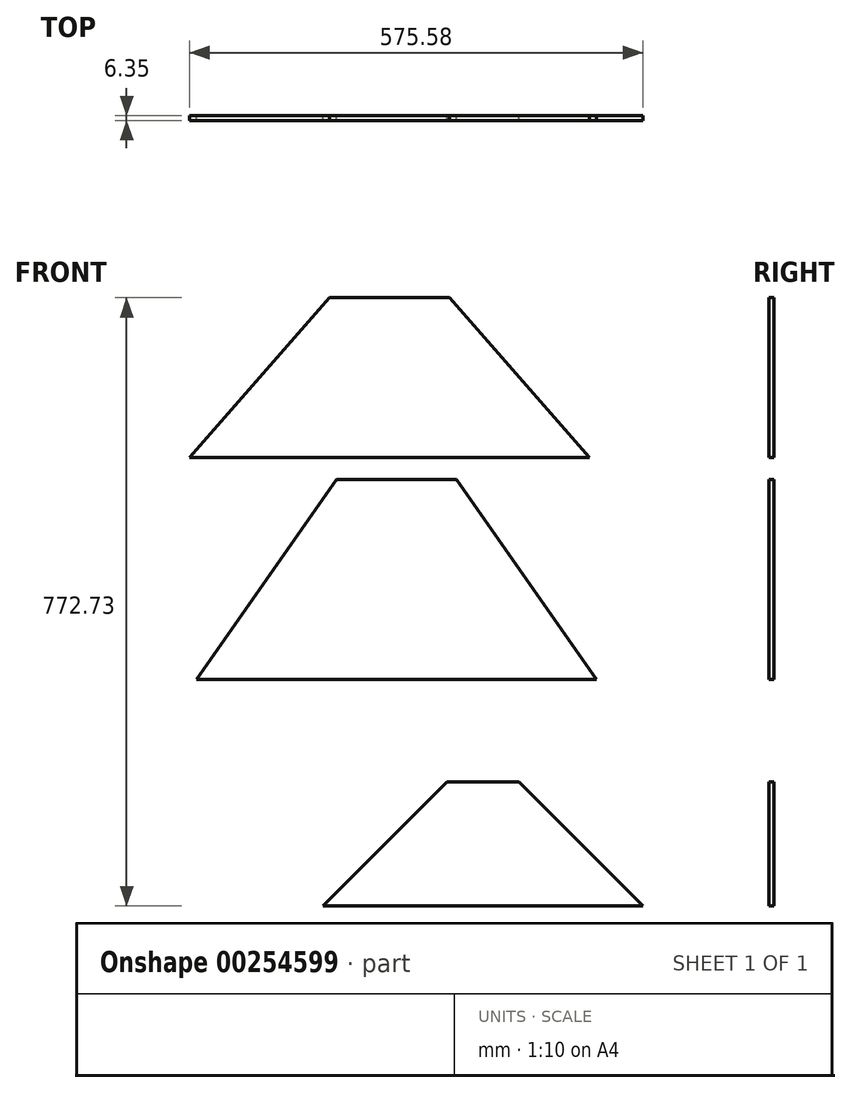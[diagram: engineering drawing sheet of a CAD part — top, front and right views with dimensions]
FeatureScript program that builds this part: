
annotation { "Feature Type Name" : "Feature", "Feature Type Description" : "" }
export const myFeature = defineFeature(function(context is Context, id is Id, definition is map)
    precondition{}
    {
        {
            var Q0;
            Q0=qCreatedBy(makeId("Front.planeOp"),FACE);
            var sketch = newSketch(context, id + "F0", { "sketchPlane" : qUnion([Q0])});
            skLineSegment(sketch, "E0", {"start": v(-249.8, -32.24) * mm, "end": v(258.2, -32.24) * mm});
            skLineSegment(sketch, "E1", {"start": v(4.2, -32.24) * mm, "end": v(4.2, 170.96) * mm, "construction": true});
            skLineSegment(sketch, "E2", {"start": v(-72, 170.96) * mm, "end": v(80.4, 170.96) * mm});
            skLineSegment(sketch, "E3", {"start": v(-249.8, -32.24) * mm, "end": v(-72, 170.96) * mm});
            skLineSegment(sketch, "E4", {"start": v(258.2, -32.24) * mm, "end": v(80.4, 170.96) * mm});
            skSolve(sketch);
        }
        {
            var Q0;
            Q0 = qSketchRegion(id + "F0", true);
            extrude(context, id + "F1", {"entities" : qUnion([Q0]), "depth" : 6.35 * mm});
        }
        {
            var Q0;
            Q0=qCreatedBy(makeId("Front.planeOp"),FACE);
            var sketch = newSketch(context, id + "F2", { "sketchPlane" : qUnion([Q0])});
            skLineSegment(sketch, "E5", {"start": v(-241.07, -314.14) * mm, "end": v(266.93, -314.14) * mm});
            skLineSegment(sketch, "E6", {"start": v(12.93, -314.14) * mm, "end": v(12.93, -60.14) * mm, "construction": true});
            skLineSegment(sketch, "E7", {"start": v(-63.27, -60.14) * mm, "end": v(89.13, -60.14) * mm});
            skLineSegment(sketch, "E8", {"start": v(-241.07, -314.14) * mm, "end": v(-63.27, -60.14) * mm});
            skLineSegment(sketch, "E9", {"start": v(89.13, -60.14) * mm, "end": v(266.93, -314.14) * mm});
            skSolve(sketch);
        }
        {
            var Q0;
            Q0 = qSketchRegion(id + "F2", true);
            extrude(context, id + "F3", {"entities" : qUnion([Q0]), "depth" : 6.35 * mm});
        }
        {
            var Q0;
            Q0=qCreatedBy(makeId("Front.planeOp"),FACE);
            var sketch = newSketch(context, id + "F4", { "sketchPlane" : qUnion([Q0])});
            skLineSegment(sketch, "E10", {"start": v(-80.63, -601.77) * mm, "end": v(325.77, -601.77) * mm});
            skLineSegment(sketch, "E11", {"start": v(122.57, -601.77) * mm, "end": v(122.57, -444.29) * mm, "construction": true});
            skLineSegment(sketch, "E12", {"start": v(76.85, -444.29) * mm, "end": v(168.3, -444.29) * mm});
            skLineSegment(sketch, "E13", {"start": v(-80.63, -601.77) * mm, "end": v(76.85, -444.29) * mm});
            skLineSegment(sketch, "E14", {"start": v(168.3, -444.29) * mm, "end": v(325.77, -601.77) * mm});
            skSolve(sketch);
        }
        {
            var Q0;
            Q0 = qSketchRegion(id + "F4", true);
            extrude(context, id + "F5", {"entities" : qUnion([Q0]), "depth" : 6.35 * mm});
        }
    });
